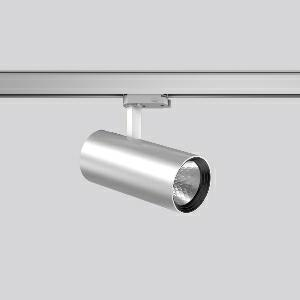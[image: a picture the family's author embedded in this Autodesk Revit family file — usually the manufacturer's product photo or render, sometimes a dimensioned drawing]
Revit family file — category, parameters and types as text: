
# Revit family: deecos_s_mini_742196_004_2_76_7122
name_source: partatom
category: Lighting Fixtures
units: mm (PartAtom-declared; Revit-internal decimal feet)

## family parameters
Cut with Voids When Loaded = No
Host = Face
Light Source = No
Part Type = Normal
Room Calculation Point = No
Round Connector Dimension = Use Diameter
Shared = No

## types (1)
- DEECOS S mini (1 x LED Modul 927, 2300 lm, 2700)
    Apparent Load = 20 VA
    Approval mark = CE
    CIE Flux Codes = 99 100 100 100 100
    Color Rendering = 92
    Color Temperature = 2700
    Default Elevation = 1800 mm
    Description = Series: DEECOS S mini
LED surface-mounted projector in modern design with no visible cooling ribs. Housing: die-cast aluminium, powder-coated. Rotation range: 356°. Swivel range: 90°. Black plastic ring and recessed LED to prevent glare from the side. Optical assembly with reflector made of MIRO-Silver with 98% total light reflection for outstanding efficiency - can be changed without tools. Best colour rendering index Ra>90. With adapter for RZB 3-circuit DALI tracks. Suitable for Track on ceiling, Wall track. High quality converter without flickering and stroboscopic effect. The following accessories can be mounted without use of tools: interchangeable lenses, decorative glasses, honeycomb louvre, clear and frosted diffusers, white interchangeable plastic ring. 
Colour: silver
Diameter: 87 mm
Height: 214 mm
Lamp: LED
Socket: without socket
Colour temperature: 2700K
Colour rendering index (CRI): 92
System power: 20 W
Rated luminous flux: 2300 lm
Luminous efficiency: 115 lm/W
Control gear: Converter, dimmable, DALI
Protection class: I
Type of protection: IP 20
    Height = 214 mm
    Lamp = 1 x LED Modul 927
    Lamp Light Flux = 2300 lm
    Lamp count = 1
    Length = 87 mm
    Lifetime = 50000 h
    Luminous efficacy = 115 lm/W
    Manufacturer = RZB
    ModVariant = No
    Model = 742196.004.2.76
    Mounting Place = Ceiling
    Mounting Type = Rail mounted
    Number of Poles = 1
    OnlyDefault = Yes
    Power Factor = 1
    Product Name = DEECOS S mini
    Product group = Track mounted projectors
    ProductGroupID = 301
    Protection Class = Protection class I
    Protection Degree = IP 20
    RLX_Detail_Level = 1
    RLX_Emergency_Light_Flux = 0 lm
    RLX_Emergency_Type = 0
    RLX_Emergency_Type_DB = No
    RlxData = <blob elided: 37185 chars, md5=71d51134>
    Socket = socket
    Standby Power = 0 W
    System Light Flux = 2300 lm
    System Power = 20 W
    Type Comments = Product without accessories
    Type Image = 741926.004.jpg
    URL = http://relux.com
    VarID = ---
    Voltage = 230 V
    Voltage Range = 220-240 V
    Weight = 0.00 kg
    Width = 0 mm  [stored 0 ft]

note: [stored X ft] marks values corroborated as IEEE doubles in the binary element streams (Revit-internal decimal feet)

## geometry (parser evidence)
native form markers: Blend x4, Sweep x11
no freeform markers — native parametric forms only
